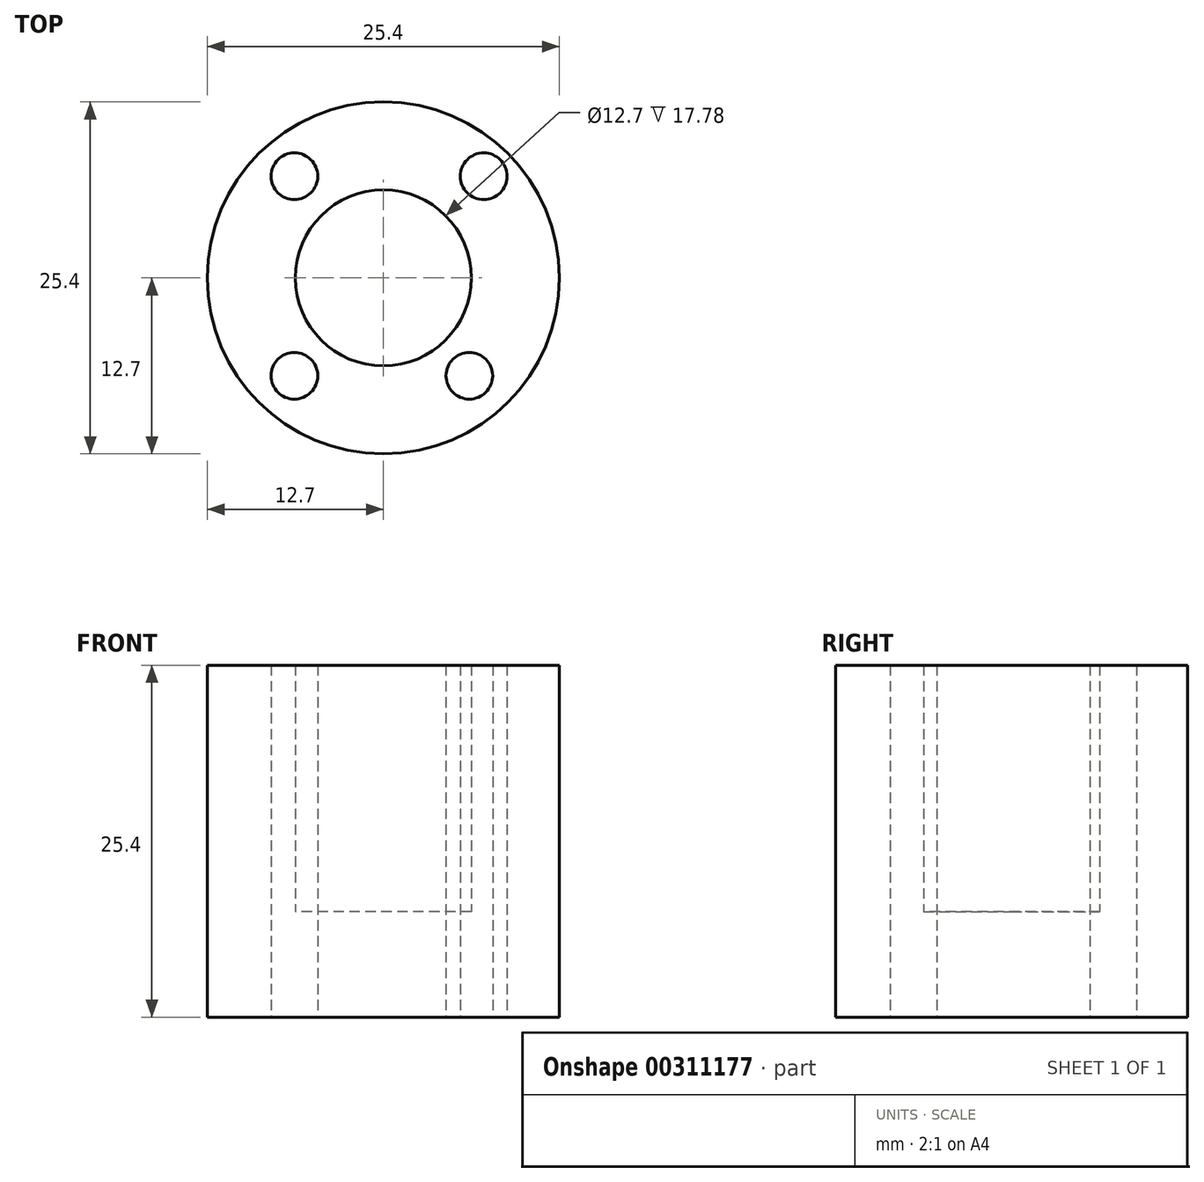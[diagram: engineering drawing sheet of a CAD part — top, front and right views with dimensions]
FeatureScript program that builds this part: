
annotation { "Feature Type Name" : "Feature", "Feature Type Description" : "" }
export const myFeature = defineFeature(function(context is Context, id is Id, definition is map)
    precondition{}
    {
        {
            var Q0;
            Q0=qCreatedBy(makeId("Top.planeOp"),FACE);
            var sketch = newSketch(context, id + "F0", { "sketchPlane" : qUnion([Q0])});
            skCircle(sketch, "E0", {"center": v(0, 0) * mm, "radius": 4 * mm});
            skCircle(sketch, "E1", {"center": v(0, 0) * mm, "radius": 6.35 * mm});
            skCircle(sketch, "E2", {"center": v(0, 0) * mm, "radius": 12.7 * mm});
            skCircle(sketch, "E3", {"center": v(-6.42, 7.34) * mm, "radius": 1.68 * mm});
            skCircle(sketch, "E4", {"center": v(7.24, 7.34) * mm, "radius": 1.68 * mm});
            skCircle(sketch, "E5", {"center": v(-6.42, -7.06) * mm, "radius": 1.68 * mm});
            skCircle(sketch, "E6", {"center": v(6.2, -7.06) * mm, "radius": 1.68 * mm});
            skCircle(sketch, "E7", {"center": v(-47.02, 29.03) * mm, "radius": 4 * mm});
            skCircle(sketch, "E8", {"center": v(-47.02, 29.03) * mm, "radius": 6.35 * mm});
            skCircle(sketch, "E9", {"center": v(-47.02, 29.03) * mm, "radius": 12.7 * mm});
            skCircle(sketch, "E10", {"center": v(-53.45, 36.37) * mm, "radius": 1.68 * mm});
            skCircle(sketch, "E11", {"center": v(-39.78, 36.37) * mm, "radius": 1.68 * mm});
            skCircle(sketch, "E12", {"center": v(-53.45, 21.97) * mm, "radius": 1.68 * mm});
            skCircle(sketch, "E13", {"center": v(-40.82, 21.97) * mm, "radius": 1.68 * mm});
            skSolve(sketch);
        }
        {
            var Q0;
            Q0=makeQuery(id+"F0.imprint","IMPRINT",FACE,{"disambiguationData":[TD([[makeQuery(id+"F0.imprint","IMPRINT",EDGE,{"derivedFrom":sQuery(id+"F0.wireOp",EDGE,"E1")}),-1.0]])]});
            extrude(context, id + "F1", {"entities" : qUnion([Q0]), "depth" : 25.4 * mm});
        }
        {
            var Q0;
            Q0=makeQuery(id+"F0.imprint","IMPRINT",FACE,{"disambiguationData":[TD([[makeQuery(id+"F0.imprint","IMPRINT",EDGE,{"derivedFrom":sQuery(id+"F0.wireOp",EDGE,"E0")}),-1.0]])]});
            extrude(context, id + "F2", {"entities" : qUnion([Q0]), "operationType" : NewBodyOperationType.ADD, "depth" : 7.62 * mm});
        }
        {
            var Q0;
            Q0=makeQuery(id+"F0.imprint","IMPRINT",FACE,{"disambiguationData":[TD([[makeQuery(id+"F0.imprint","IMPRINT",EDGE,{"derivedFrom":sQuery(id+"F0.wireOp",EDGE,"E0")}),1.0]])]});
            extrude(context, id + "F3", {"entities" : qUnion([Q0]), "operationType" : NewBodyOperationType.ADD, "depth" : 7.62 * mm});
        }
    });
